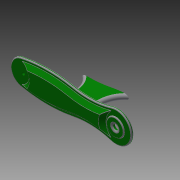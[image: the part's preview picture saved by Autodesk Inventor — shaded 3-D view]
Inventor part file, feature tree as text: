
AUTODESK INVENTOR PART (.ipt)
format: ipt  version: 2015 (Build 190159000, 159)  size: 631,808 bytes
history: native  units: mm
features: extrude x16, sketch x15, fillet x5, chamfer x2
ambient origin geometry x8: Origin, YZ Plane, XZ Plane, XY Plane, X Axis, Y Axis, Z Axis, Center Point
bodies: Solid1 (feature_tree)
feature tree (38):
  extrude  "Extrusion1"  Depth=50.0mm
  extrude  "Extrusion2"  Depth=15.0mm
  extrude  "Extrusion3"  Depth=5.0mm TaperAngle=0.0deg
  extrude  "Extrusion4"  Depth=18.1mm
  extrude  "Extrusion5"  Depth=20.0mm
  extrude  "Extrusion6"  Depth=9.5mm
  sketch  "Sketch7"  dims[d15=9.9mm d16=9.5mm]
  extrude  "Extrusion7"  Depth=9.5mm
  chamfer  "Chamfer1"  Distance=5.0mm
  extrude  "Extrusion8"  Depth=2.0mm
  extrude  "Extrusion17"  Depth=5.0mm TaperAngle=0.0deg
  chamfer  "Chamfer2"  Distance=5.0mm
  extrude  "Extrusion25"  Depth=5.0mm TaperAngle=0.0deg
  extrude  "Extrusion26"  Depth=20.0mm
  extrude  "Extrusion27"  Depth=30.0mm
  sketch  "Sketch30"  dims[d26=2.0mm d29=2.0mm]
  extrude  "Extrusion28"  Depth=7.3mm TaperAngle=0.0deg
  extrude  "Extrusion32"  Depth=7.3mm TaperAngle=45.0deg
  extrude  "Extrusion33"  Depth=12.3mm TaperAngle=0.0deg
  extrude  "Extrusion34"  Depth=6.0mm
  fillet  "Fillet5"  Radius=5.0mm
  fillet  "Fillet6"  Radius=7.3mm
  fillet  "Fillet7"  Radius=35.0mm
  fillet  "Fillet8"  Radius=2.0mm
  fillet  "Fillet9"  Radius=10.0mm
  sketch  "Sketch1"  dims[d0=180.0mm d1=50.0mm]
  sketch  "Sketch2"  dims[d2=5.0mm d3=0.0mm d4=15.0mm]
  sketch  "Sketch3"  dims[d5=15.0mm d6=5.0mm d7=0.0mm]
  sketch  "Sketch4"  dims[d9=34.65mm d10=18.1mm]
  sketch  "Sketch5"  dims[d11=55.0mm d12=20.0mm]
  sketch  "Sketch6"  dims[d13=40.2mm d14=9.5mm]
  sketch  "Sketch8"  dims[d17=9.9mm]
  sketch  "Sketch9"  dims[d18=3.0mm]
  sketch  "Sketch18"  dims[d19=3.0mm]
  sketch  "Sketch27"  dims[d20=3.0mm]
  sketch  "Sketch28"  dims[d21=3.0mm]
  sketch  "Sketch29"  dims[d22=13.6mm d23=5.0mm d24=0.0mm]
  sketch  "Sketch33"  dims[d30=2.0mm d31=5.0mm d32=0.0mm d63=5.0mm d64=0.0mm d65=5.0mm d66=0.0mm d72=20.0mm d73=30.0mm d74=7.3mm d75=0.0mm d76=7.3mm d77=2.0mm d78=45.0deg d79=12.3mm d80=0.0mm d114=6.0mm d115=5.0mm d116=0.0mm d117=7.3mm d118=2.0mm d119=45.0deg d155=35.0mm d156=2.0mm d157=0.0mm d158=10.0mm d159=2.0mm d160=0.0mm d161=5.0mm d162=0.0mm d177=72.6mm d178=0.0mm d183=20.0mm d184=80.0mm d192=80.0mm d195=10.0mm d196=20.0mm d197=10.0mm d199=72.6mm d200=0.0mm d201=45.0mm d202=45.0mm d203=20.0mm d204=0.0mm d205=72.6mm d206=0.0mm d211=2.0mm d212=5.0mm d213=2.0mm d214=1.0mm d215=5.0mm]
